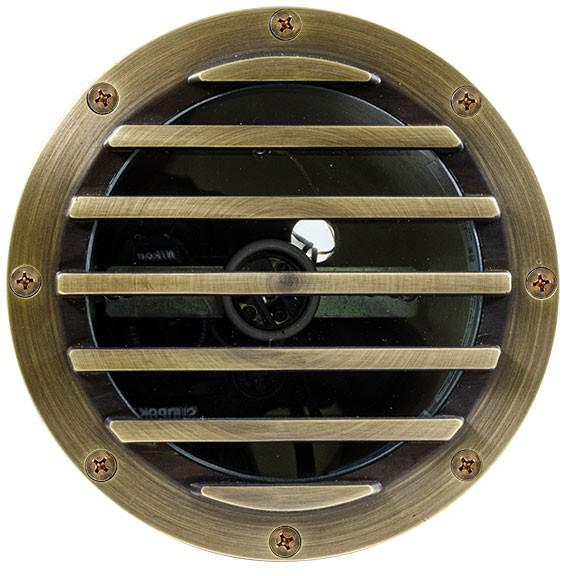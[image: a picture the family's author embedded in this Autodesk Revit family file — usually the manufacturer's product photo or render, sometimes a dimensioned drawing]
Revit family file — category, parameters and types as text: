
# Revit family: Alcon-9042-Revit-Family
name_source: partatom
category: Luminarias
units: mm (PartAtom-declared; Revit-internal decimal feet)

## family parameters
Anfitrión = Cara
Compartido = No
Corte con vacíos al cargar = No
Cota de conector redondo = Usar diámetro
Mantener orientación de anotación = No
Origen de luz = Sí
Punto de cálculo de habitación = No
Tipo de pieza = Normal

## types (1)
- Alcon-9042-Revit-Family
    Cambio de temperatura de color de luz atenuada = <Ninguno>
    Elevación por defecto = 4' - 0"
    Fabricante = Alcon Lighting
    Filtro de color = 16777215
    GLASS LENS = Analytical Panels
    HOUSING = <Por categoría>
    LENS GLASS = Glass
    Link to IES File = https://www.alconlighting.com
    Longitud de símbolo de origen de luz = 10' - 0"
    Modelo = Alcon Lighting 9034-9
    Product Data URL = https://www.alconlighting.com
    Product Page = https://www.alconlighting.com
    TAP LENS = <Por categoría>
    TOP FINISH = <Por categoría>
    URL = https://www.alconlighting.com
    Ángulo de campo de foco = 90.00°
    Ángulo de enfoque = 30.00°
    Ángulo de inclinación = 60.00°

## geometry (parser evidence)
native form markers: Sweep x2
no freeform markers — native parametric forms only
